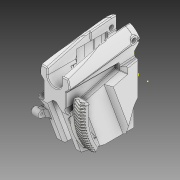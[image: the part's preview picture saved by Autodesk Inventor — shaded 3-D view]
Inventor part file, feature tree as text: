
AUTODESK INVENTOR PART (.ipt)
format: ipt  version: 2020 (Build 240168000, 168)  size: 3,878,400 bytes
history: native  units: in
note: dims shown in document units (in); Inventor stores cm internally (conversion verified against a paired STEP export)
features: sketch x10, extrude x9, fillet x4, other x3, chamfer x2, projected_geometry x2
ambient origin geometry x8: Origin, YZ Plane, XZ Plane, XY Plane, X Axis, Y Axis, Z Axis, Center Point
bodies: Solid1 (feature_tree)
feature tree (30):
  other  "GearedUpper.iam"
  other  "EUpper_Alt.ipt:1"
  other  "144 Tooth Herringbone semicircle.ipt:1"
  extrude  "Extrusion1"  Depth=0.0687in
  extrude  "Extrusion2"  Depth=1.0in TaperAngle=0.0deg
  extrude  "Extrusion3"  Depth=1.0in TaperAngle=0.0deg
  extrude  "Extrusion4"  Depth=1.0in TaperAngle=0.0deg
  extrude  "Extrusion5"  Depth=0.3937in TaperAngle=0.0deg
  extrude  "Extrusion6"  Depth=0.0787in
  fillet  "Fillet1"  Radius=3.4646in
  fillet  "Fillet2"  Radius=2.2047in
  sketch  "Sketch12"  dims[d29=0.315in]
  extrude  "Extrusion7"  Depth=1.7717in
  extrude  "Extrusion8"  Depth=1.9291in
  fillet  "Fillet3"  Radius=2.2835in
  fillet  "Fillet4"  Radius=0.0965in
  chamfer  "Chamfer1"  Distance=0.2756in
  extrude  "Extrusion9"  Depth=0.0394in TaperAngle=0.0deg
  chamfer  "Chamfer2"  Distance=0.0787in
  sketch  "Sketch4"  dims[d2=0.2405in d3=1.0in d4=0.0in]
  sketch  "Sketch9"  dims[d23=0.0756in d24=1.7717in]
  sketch  "Sketch3"  dims[d0=0.3937in d1=0.0687in]
  sketch  "Sketch5"  dims[d5=1.0in d6=0.0in d7=1.0in d8=0.0in]
  sketch  "Sketch6"  dims[d10=0.1575in d11=1.0in d12=0.0in]
  projected_geometry  "Projected Loop1"
  sketch  "Sketch7"  dims[d13=0.0in d14=0.0in d15=0.3937in d16=0.0in]
  sketch  "Sketch8"  dims[d17=0.1969in d18=0.0787in d21=3.4646in d22=2.2047in]
  sketch  "Sketch10"  dims[d25=2.7953in d26=1.9291in d27=2.2835in d28=0.0965in]
  projected_geometry  "Projected Loop2"
  sketch  "Sketch13"  dims[d30=0.315in d31=0.2756in d32=0.3937in d33=0.0in d34=0.0787in d35=0.5906in d36=0.1969in d37=0.0in d38=0.1575in d39=0.1181in d40=0.1181in d41=0.0591in d42=0.0787in d43=45.0deg d44=0.0394in d45=0.1969in d46=0.0in d47=0.0787in d48=0.0787in d49=45.0deg]
